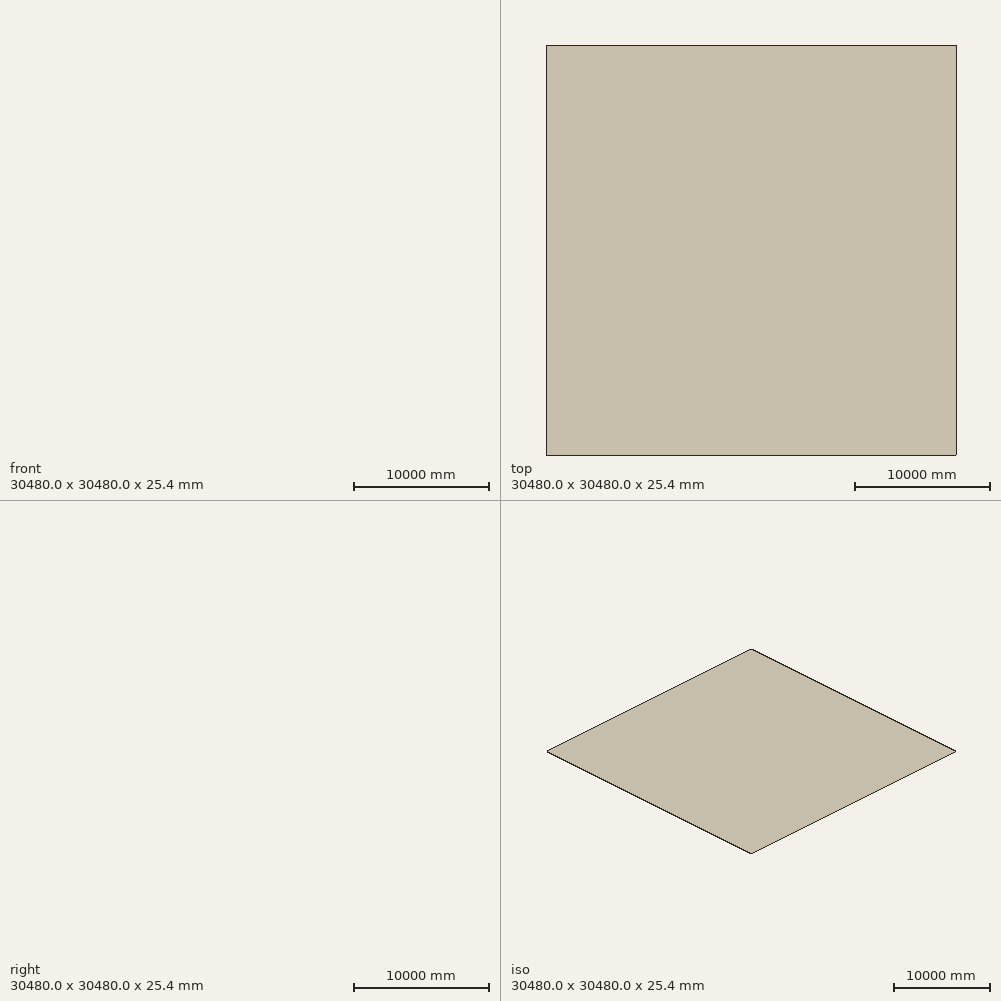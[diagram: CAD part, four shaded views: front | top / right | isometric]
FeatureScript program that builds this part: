
annotation { "Feature Type Name" : "Feature", "Feature Type Description" : "" }
export const myFeature = defineFeature(function(context is Context, id is Id, definition is map)
    precondition{}
    {
        {
            var Q0;
            Q0=qCreatedBy(makeId("Top.planeOp"),FACE);
            var sketch = newSketch(context, id + "F0", { "sketchPlane" : qUnion([Q0])});
            skLineSegment(sketch, "E0.bottom", {"start": v(-15281.68, 24100.17) * mm, "end": v(15198.32, 24100.17) * mm});
            skLineSegment(sketch, "E0.top", {"start": v(-15281.68, -6379.83) * mm, "end": v(15198.32, -6379.83) * mm});
            skLineSegment(sketch, "E0.left", {"start": v(-15281.68, 24100.17) * mm, "end": v(-15281.68, -6379.83) * mm});
            skLineSegment(sketch, "E0.right", {"start": v(15198.32, 24100.17) * mm, "end": v(15198.32, -6379.83) * mm});
            skSolve(sketch);
        }
        {
            var Q0;
            Q0 = qSketchRegion(id + "F0", true);
            extrude(context, id + "F1", {"entities" : qUnion([Q0]), "depth" : 25.4 * mm});
        }
    });
